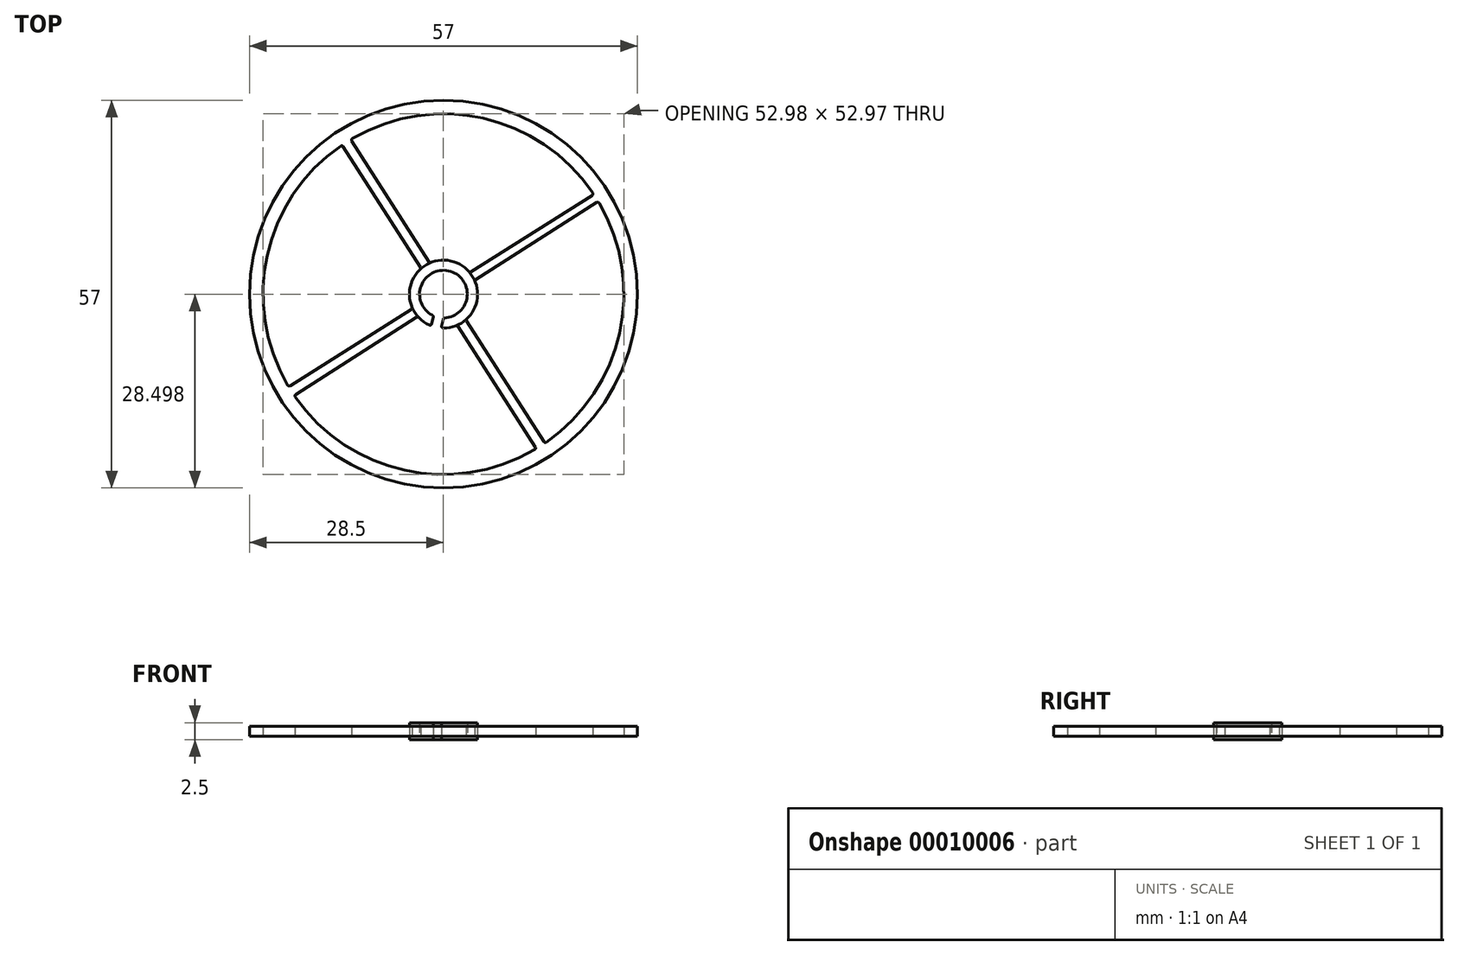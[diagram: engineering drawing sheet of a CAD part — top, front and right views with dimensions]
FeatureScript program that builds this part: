
annotation { "Feature Type Name" : "Feature", "Feature Type Description" : "" }
export const myFeature = defineFeature(function(context is Context, id is Id, definition is map)
    precondition{}
    {
        {
            var Q0;
            Q0=qCreatedBy(makeId("Top.planeOp"),FACE);
            var sketch = newSketch(context, id + "F0", { "sketchPlane" : qUnion([Q0])});
            skCircle(sketch, "E0", {"center": v(0, 0) * mm, "radius": 28.5 * mm});
            skArc(sketch, "E1.0", {"start": v(21.92, 14.89) * mm, "mid": v(5.84, 25.85) * mm, "end": v(-13.4, 22.87) * mm});
            skArc(sketch, "E2", {"start": v(0.19, -3.5) * mm, "mid": v(3.47, -0.46) * mm, "end": v(1.08, 3.33) * mm});
            skArc(sketch, "E3.0", {"start": v(3.72, 3.34) * mm, "mid": v(3, 4) * mm, "end": v(2.15, 4.51) * mm});
            skLineSegment(sketch, "E4.0", {"start": v(14.74, -21.7) * mm, "end": v(3.4, -3.94) * mm});
            skLineSegment(sketch, "E5.0.MirrorCS", {"start": v(13.5, -22.5) * mm, "end": v(2.15, -4.74) * mm});
            skLineSegment(sketch, "E6.0", {"start": v(-21.7, -14.74) * mm, "end": v(-3.94, -3.4) * mm});
            skLineSegment(sketch, "E7.0.MirrorCS", {"start": v(-22.52, -13.48) * mm, "end": v(-4.71, -2.23) * mm});
            skLineSegment(sketch, "E8.trimOffspring", {"start": v(4.04, 3.3) * mm, "end": v(21.85, 14.54) * mm});
            skLineSegment(sketch, "E9.trimOffspring", {"start": v(4.75, 2.14) * mm, "end": v(22.52, 13.48) * mm});
            skLineSegment(sketch, "E10.trimOffspring", {"start": v(-2.14, 4.75) * mm, "end": v(-13.48, 22.52) * mm});
            skLineSegment(sketch, "E11.trimOffspring", {"start": v(-3.4, 3.95) * mm, "end": v(-14.74, 21.7) * mm});
            skArc(sketch, "E12.trimOffspring", {"start": v(3.44, -3.63) * mm, "mid": v(4.88, -1.08) * mm, "end": v(4.65, 1.84) * mm});
            skArc(sketch, "E13.trimOffspring", {"start": v(-3.63, -3.44) * mm, "mid": v(-2.9, -4.07) * mm, "end": v(-2.08, -4.55) * mm});
            skArc(sketch, "E14.trimOffspring", {"start": v(-3.44, 3.63) * mm, "mid": v(-4.9, 1.04) * mm, "end": v(-4.61, -1.93) * mm});
            skArc(sketch, "E15.trimOffspring", {"start": v(15.1, -21.78) * mm, "mid": v(25.88, -5.72) * mm, "end": v(22.87, 13.4) * mm});
            skArc(sketch, "E16.trimOffspring", {"start": v(-21.78, -15.1) * mm, "mid": v(-5.7, -25.88) * mm, "end": v(13.41, -22.85) * mm});
            skArc(sketch, "E17.trimOffspring", {"start": v(-15.1, 21.78) * mm, "mid": v(-25.88, 5.72) * mm, "end": v(-22.87, -13.4) * mm});
            skLineSegment(sketch, "E18.0", {"start": v(-1.5, -3.37) * mm, "end": v(-1.73, -4.37) * mm});
            skLineSegment(sketch, "E19.0.MirrorCS", {"start": v(-0.04, -3.7) * mm, "end": v(-0.26, -4.7) * mm});
            skArc(sketch, "E20.trimOffspring", {"start": v(-0.02, -5) * mm, "mid": v(0.93, -4.91) * mm, "end": v(1.85, -4.64) * mm});
            skArc(sketch, "E21.trimOffspring", {"start": v(1.08, 3.33) * mm, "mid": v(-3.22, 1.36) * mm, "end": v(-1.63, -3.1) * mm});
            skArc(sketch, "E22.trimOffspring", {"start": v(2.15, 4.51) * mm, "mid": v(0.17, 5) * mm, "end": v(-1.84, 4.65) * mm});
            skPoint(sketch, "E23.visualSharp", {"position": v(-1.47, -3.18) * mm});
            skArc(sketch, "E23.filletArc", {"start": v(-1.5, -3.37) * mm, "mid": v(-1.52, -3.21) * mm, "end": v(-1.63, -3.1) * mm});
            skPoint(sketch, "E24.visualSharp", {"position": v(-1.8, -4.67) * mm});
            skArc(sketch, "E24.filletArc", {"start": v(-2.08, -4.55) * mm, "mid": v(-1.86, -4.55) * mm, "end": v(-1.73, -4.37) * mm});
            skPoint(sketch, "E25.visualSharp", {"position": v(-0.33, -4.99) * mm});
            skArc(sketch, "E25.filletArc", {"start": v(-0.26, -4.7) * mm, "mid": v(-0.21, -4.9) * mm, "end": v(-0.02, -5) * mm});
            skPoint(sketch, "E26.visualSharp", {"position": v(0, -3.5) * mm});
            skArc(sketch, "E26.filletArc", {"start": v(0.19, -3.5) * mm, "mid": v(0.04, -3.55) * mm, "end": v(-0.04, -3.7) * mm});
            skPoint(sketch, "E27.visualSharp", {"position": v(-3.76, -3.3) * mm});
            skArc(sketch, "E27.filletArc", {"start": v(-3.63, -3.44) * mm, "mid": v(-3.78, -3.37) * mm, "end": v(-3.94, -3.4) * mm});
            skPoint(sketch, "E28.visualSharp", {"position": v(-4.53, -2.12) * mm});
            skArc(sketch, "E28.filletArc", {"start": v(-4.71, -2.23) * mm, "mid": v(-4.6, -2.1) * mm, "end": v(-4.61, -1.93) * mm});
            skPoint(sketch, "E29.visualSharp", {"position": v(-3.28, 3.77) * mm});
            skArc(sketch, "E29.filletArc", {"start": v(-3.44, 3.63) * mm, "mid": v(-3.36, 3.78) * mm, "end": v(-3.4, 3.95) * mm});
            skPoint(sketch, "E30.visualSharp", {"position": v(-2.03, 4.57) * mm});
            skArc(sketch, "E30.filletArc", {"start": v(-2.14, 4.75) * mm, "mid": v(-2, 4.64) * mm, "end": v(-1.84, 4.65) * mm});
            skPoint(sketch, "E31.visualSharp", {"position": v(3.86, 3.18) * mm});
            skArc(sketch, "E31.filletArc", {"start": v(3.72, 3.34) * mm, "mid": v(3.87, 3.26) * mm, "end": v(4.04, 3.3) * mm});
            skPoint(sketch, "E32.visualSharp", {"position": v(4.57, 2.03) * mm});
            skArc(sketch, "E32.filletArc", {"start": v(4.75, 2.14) * mm, "mid": v(4.64, 2) * mm, "end": v(4.65, 1.84) * mm});
            skPoint(sketch, "E33.visualSharp", {"position": v(3.3, -3.76) * mm});
            skArc(sketch, "E33.filletArc", {"start": v(3.44, -3.63) * mm, "mid": v(3.37, -3.78) * mm, "end": v(3.4, -3.94) * mm});
            skPoint(sketch, "E34.visualSharp", {"position": v(2.04, -4.56) * mm});
            skArc(sketch, "E34.filletArc", {"start": v(2.15, -4.74) * mm, "mid": v(2.02, -4.64) * mm, "end": v(1.85, -4.64) * mm});
            skArc(sketch, "E35.filletArc", {"start": v(-22.87, -13.4) * mm, "mid": v(-22.7, -13.51) * mm, "end": v(-22.52, -13.48) * mm});
            skArc(sketch, "E36.filletArc", {"start": v(-21.7, -14.74) * mm, "mid": v(-21.82, -14.9) * mm, "end": v(-21.78, -15.1) * mm});
            skArc(sketch, "E37.filletArc", {"start": v(13.41, -22.85) * mm, "mid": v(13.53, -22.7) * mm, "end": v(13.5, -22.5) * mm});
            skArc(sketch, "E38.filletArc", {"start": v(14.74, -21.7) * mm, "mid": v(14.9, -21.82) * mm, "end": v(15.1, -21.78) * mm});
            skArc(sketch, "E39.filletArc", {"start": v(22.87, 13.4) * mm, "mid": v(22.7, 13.51) * mm, "end": v(22.52, 13.48) * mm});
            skPoint(sketch, "E40.visualSharp", {"position": v(22.07, 14.68) * mm});
            skArc(sketch, "E40.filletArc", {"start": v(21.85, 14.54) * mm, "mid": v(21.96, 14.7) * mm, "end": v(21.92, 14.89) * mm});
            skArc(sketch, "E41.filletArc", {"start": v(-13.4, 22.87) * mm, "mid": v(-13.51, 22.7) * mm, "end": v(-13.48, 22.52) * mm});
            skArc(sketch, "E42.filletArc", {"start": v(-14.74, 21.7) * mm, "mid": v(-14.9, 21.82) * mm, "end": v(-15.1, 21.78) * mm});
            skSolve(sketch);
        }
        {
            var Q0;
            Q0 = qSketchRegion(id + "F0", true);
            extrude(context, id + "F1", {"entities" : qUnion([Q0]), "depth" : 1.5 * mm});
        }
        {
            var Q0;
            Q0=makeQuery(id+"F1.opExtrude","CAP_FACE",FACE,{"disambiguationData":[OSD([sQuery(id+"F0.wireOp",EDGE,"E0"),sQuery(id+"F0.wireOp",EDGE,"E1.0"),sQuery(id+"F0.wireOp",EDGE,"E2"),sQuery(id+"F0.wireOp",EDGE,"E3.0"),sQuery(id+"F0.wireOp",EDGE,"E4.0"),sQuery(id+"F0.wireOp",EDGE,"E5.0.MirrorCS"),sQuery(id+"F0.wireOp",EDGE,"E6.0"),sQuery(id+"F0.wireOp",EDGE,"E7.0.MirrorCS"),sQuery(id+"F0.wireOp",EDGE,"E8.trimOffspring"),sQuery(id+"F0.wireOp",EDGE,"E9.trimOffspring"),sQuery(id+"F0.wireOp",EDGE,"E10.trimOffspring"),sQuery(id+"F0.wireOp",EDGE,"E11.trimOffspring"),sQuery(id+"F0.wireOp",EDGE,"E12.trimOffspring"),sQuery(id+"F0.wireOp",EDGE,"E13.trimOffspring"),sQuery(id+"F0.wireOp",EDGE,"E14.trimOffspring"),sQuery(id+"F0.wireOp",EDGE,"E15.trimOffspring"),sQuery(id+"F0.wireOp",EDGE,"E16.trimOffspring"),sQuery(id+"F0.wireOp",EDGE,"E17.trimOffspring"),sQuery(id+"F0.wireOp",EDGE,"E18.0"),sQuery(id+"F0.wireOp",EDGE,"E19.0.MirrorCS"),sQuery(id+"F0.wireOp",EDGE,"E20.trimOffspring"),sQuery(id+"F0.wireOp",EDGE,"E21.trimOffspring"),sQuery(id+"F0.wireOp",EDGE,"E22.trimOffspring"),sQuery(id+"F0.wireOp",EDGE,"E23.filletArc"),sQuery(id+"F0.wireOp",EDGE,"E24.filletArc"),sQuery(id+"F0.wireOp",EDGE,"E25.filletArc"),sQuery(id+"F0.wireOp",EDGE,"E26.filletArc"),sQuery(id+"F0.wireOp",EDGE,"E27.filletArc"),sQuery(id+"F0.wireOp",EDGE,"E28.filletArc"),sQuery(id+"F0.wireOp",EDGE,"E29.filletArc"),sQuery(id+"F0.wireOp",EDGE,"E30.filletArc"),sQuery(id+"F0.wireOp",EDGE,"E31.filletArc"),sQuery(id+"F0.wireOp",EDGE,"E32.filletArc"),sQuery(id+"F0.wireOp",EDGE,"E33.filletArc"),sQuery(id+"F0.wireOp",EDGE,"E34.filletArc"),sQuery(id+"F0.wireOp",EDGE,"E35.filletArc"),sQuery(id+"F0.wireOp",EDGE,"E36.filletArc"),sQuery(id+"F0.wireOp",EDGE,"E37.filletArc"),sQuery(id+"F0.wireOp",EDGE,"E38.filletArc"),sQuery(id+"F0.wireOp",EDGE,"E39.filletArc"),sQuery(id+"F0.wireOp",EDGE,"E40.filletArc"),sQuery(id+"F0.wireOp",EDGE,"E41.filletArc"),sQuery(id+"F0.wireOp",EDGE,"E42.filletArc")])],"isStart":false});
            var sketch = newSketch(context, id + "F2", { "sketchPlane" : qUnion([Q0])});
            skArc(sketch, "E43", {"start": v(0.19, -3.5) * mm, "mid": v(3.47, -0.46) * mm, "end": v(1.08, 3.33) * mm});
            skArc(sketch, "E44.0", {"start": v(3.72, 3.34) * mm, "mid": v(3, 4) * mm, "end": v(2.15, 4.51) * mm});
            skArc(sketch, "E45.trimOffspring", {"start": v(1.85, -4.64) * mm, "mid": v(4.87, -1.14) * mm, "end": v(3.72, 3.34) * mm});
            skArc(sketch, "E46.trimOffspring", {"start": v(-4.61, -1.93) * mm, "mid": v(-3.6, -3.48) * mm, "end": v(-2.08, -4.55) * mm});
            skArc(sketch, "E47.trimOffspring", {"start": v(-3.44, 3.63) * mm, "mid": v(-4.9, 1.04) * mm, "end": v(-4.61, -1.93) * mm});
            skLineSegment(sketch, "E48.0", {"start": v(-1.5, -3.37) * mm, "end": v(-1.73, -4.37) * mm});
            skLineSegment(sketch, "E49.0.MirrorCS", {"start": v(-0.04, -3.7) * mm, "end": v(-0.26, -4.7) * mm});
            skArc(sketch, "E50.trimOffspring", {"start": v(-0.02, -5) * mm, "mid": v(0.93, -4.91) * mm, "end": v(1.85, -4.64) * mm});
            skArc(sketch, "E51.trimOffspring", {"start": v(1.08, 3.33) * mm, "mid": v(-3.22, 1.36) * mm, "end": v(-1.63, -3.1) * mm});
            skArc(sketch, "E52.trimOffspring", {"start": v(2.15, 4.51) * mm, "mid": v(-0.78, 4.94) * mm, "end": v(-3.44, 3.63) * mm});
            skPoint(sketch, "E53.visualSharp", {"position": v(-1.47, -3.18) * mm});
            skArc(sketch, "E53.filletArc", {"start": v(-1.5, -3.37) * mm, "mid": v(-1.52, -3.21) * mm, "end": v(-1.63, -3.1) * mm});
            skPoint(sketch, "E54.visualSharp", {"position": v(-1.8, -4.67) * mm});
            skArc(sketch, "E54.filletArc", {"start": v(-2.08, -4.55) * mm, "mid": v(-1.86, -4.55) * mm, "end": v(-1.73, -4.37) * mm});
            skPoint(sketch, "E55.visualSharp", {"position": v(-0.33, -4.99) * mm});
            skArc(sketch, "E55.filletArc", {"start": v(-0.26, -4.7) * mm, "mid": v(-0.21, -4.9) * mm, "end": v(-0.02, -5) * mm});
            skPoint(sketch, "E56.visualSharp", {"position": v(0, -3.5) * mm});
            skArc(sketch, "E56.filletArc", {"start": v(0.19, -3.5) * mm, "mid": v(0.04, -3.55) * mm, "end": v(-0.04, -3.7) * mm});
            skSolve(sketch);
        }
        {
            var Q0;
            Q0 = qSketchRegion(id + "F2", true);
            extrude(context, id + "F3", {"entities" : qUnion([Q0]), "operationType" : NewBodyOperationType.ADD, "depth" : 0.5 * mm, "hasSecondDirection" : true, "secondDirectionOppositeDirection" : true, "secondDirectionDepth" : 2 * mm});
        }
    });
